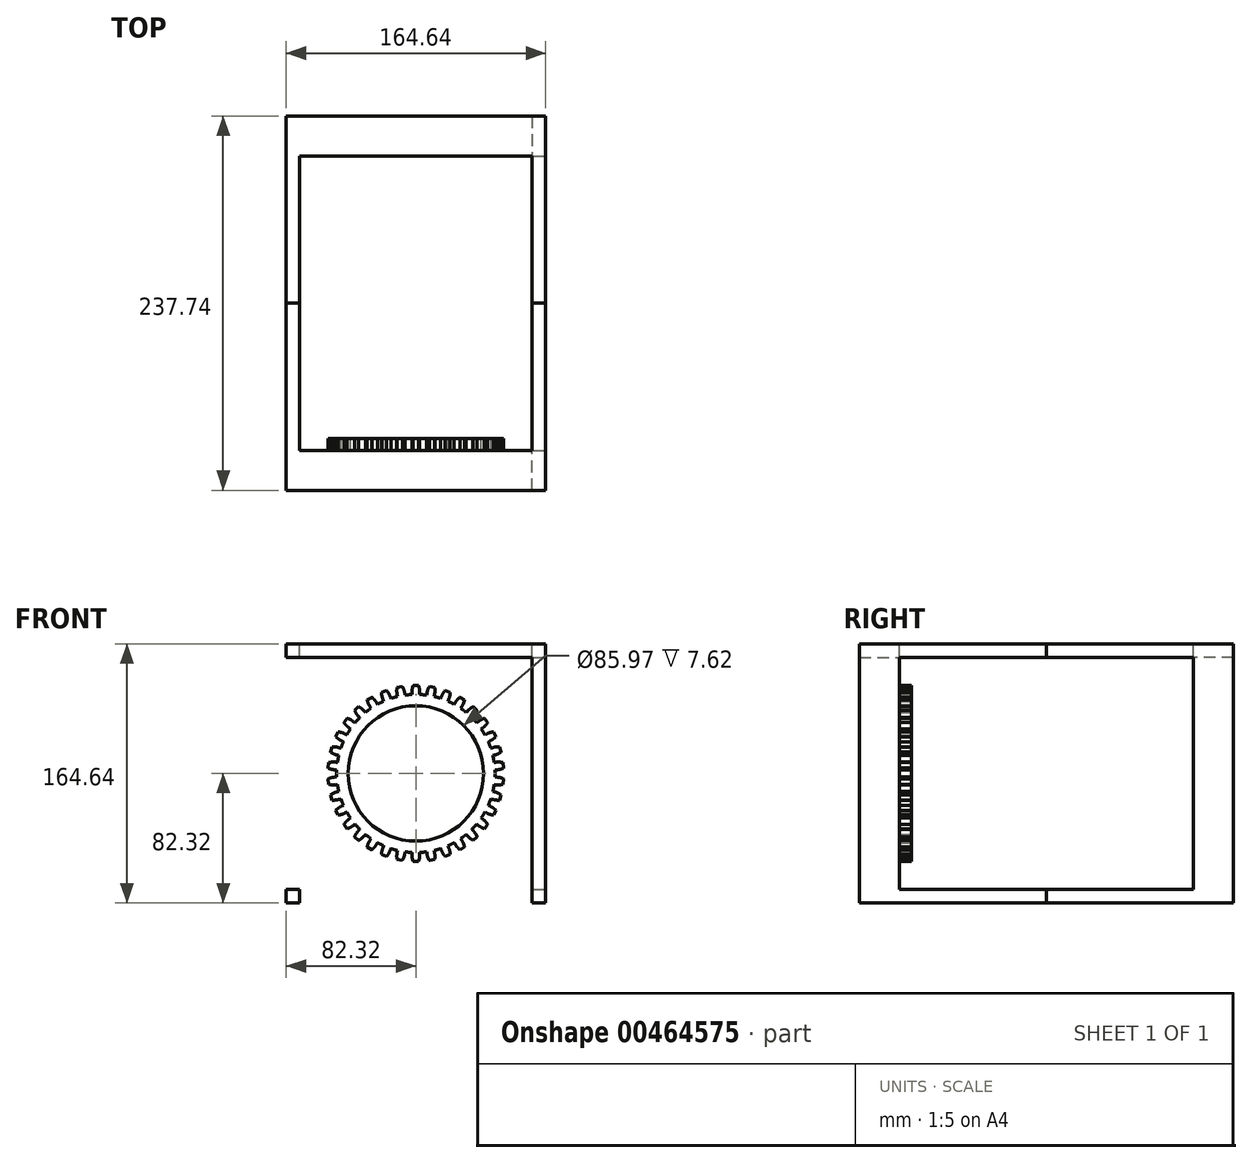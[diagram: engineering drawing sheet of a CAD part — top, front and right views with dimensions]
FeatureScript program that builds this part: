
annotation { "Feature Type Name" : "Feature", "Feature Type Description" : "" }
export const myFeature = defineFeature(function(context is Context, id is Id, definition is map)
    precondition{}
    {
        {
            var Q0;
            Q0=qCreatedBy(makeId("Front.planeOp"),FACE);
            var sketch = newSketch(context, id + "F0", { "sketchPlane" : qUnion([Q0])});
            skCircle(sketch, "E0", {"center": v(0, 0) * mm, "radius": 49.85 * mm});
            skLineSegment(sketch, "E1.bottom", {"start": v(-2.44, 49.79) * mm, "end": v(0, 49.79) * mm});
            skLineSegment(sketch, "E1.top", {"start": v(-2.44, 55.9) * mm, "end": v(0, 55.9) * mm});
            skLineSegment(sketch, "E1.left", {"start": v(-2.44, 49.79) * mm, "end": v(-2.44, 55.9) * mm});
            skLineSegment(sketch, "E1.right", {"start": v(0, 49.79) * mm, "end": v(0, 55.9) * mm});
            skFitSpline(sketch, "E2", {"points": [v(-1.74, 55.9) * mm, v(-2.44, 51.25) * mm], "startDerivative": vector(-1.37, -5.09) * mm, "endDerivative": vector(0, -7.68) * mm});
            skLineSegment(sketch, "E3.MirrorCS", {"start": v(2.44, 55.9) * mm, "end": v(0, 55.9) * mm});
            skFitSpline(sketch, "E4.MirrorCS", {"points": [v(1.74, 55.9) * mm, v(2.44, 51.25) * mm], "startDerivative": vector(1.37, -5.09) * mm, "endDerivative": vector(0, -7.68) * mm});
            skLineSegment(sketch, "E5.MirrorCS", {"start": v(2.44, 49.79) * mm, "end": v(2.44, 55.9) * mm});
            skCircle(sketch, "E6", {"center": v(0, 0) * mm, "radius": 50.24 * mm});
            skCircle(sketch, "E7", {"center": v(0, 0) * mm, "radius": 42.98 * mm});
            skSolve(sketch);
        }
        {
            var Q0;
            {var subQ5=sQuery(id+"F0.wireOp",EDGE,"E2");Q0=makeQuery(id+"F0.imprint","IMPRINT",FACE,{"disambiguationData":[TD([[makeQuery(id+"F0.imprint","IMPRINT",EDGE,{"derivedFrom":subQ5}),1.0]])]});}
            var Q1;
            {var subQ0=sQuery(id+"F0.wireOp",EDGE,"E4.MirrorCS");Q1=makeQuery(id+"F0.imprint","IMPRINT",FACE,{"disambiguationData":[TD([[makeQuery(id+"F0.imprint","IMPRINT",EDGE,{"derivedFrom":subQ0}),-1.0]])]});}
            extrude(context, id + "F1", {"entities" : qUnion([Q0, Q1]), "depth" : 7.62 * mm});
        }
        {
            var Q0;
            Q0=qCreatedBy(makeId("Top.planeOp"),FACE);
            var sketch = newSketch(context, id + "F2", { "sketchPlane" : qUnion([Q0])});
            skLineSegment(sketch, "E8", {"start": v(0, 0) * mm, "end": v(0, -26.55) * mm});
            skSolve(sketch);
        }
        {
            var Q0;
            Q0=makeQuery(id+"F1.opExtrude","SWEPT_BODY",BODY,{"disambiguationData":[OSD([sQuery(id+"F0.wireOp",EDGE,"E0"),sQuery(id+"F0.wireOp",EDGE,"E1.top"),sQuery(id+"F0.wireOp",EDGE,"E1.left"),sQuery(id+"F0.wireOp",EDGE,"E2"),sQuery(id+"F0.wireOp",EDGE,"E3.MirrorCS"),sQuery(id+"F0.wireOp",EDGE,"E4.MirrorCS"),sQuery(id+"F0.wireOp",EDGE,"E5.MirrorCS")])]});
            var Q1;
            Q1=sQuery(id+"F2.wireOp",EDGE,"E8");
            circularPattern(context, id + "F3", {"entities" : qUnion([Q0]), "axis" : qUnion([Q1]), "angle" : 360 * degree, "instanceCount" : 34, "equalSpace" : true});
        }
        {
            var Q0;
            {var subQ1=sQuery(id+"F0.wireOp",EDGE,"E0");var subQ3=sQuery(id+"F0.wireOp",EDGE,"E5.MirrorCS");var subQ4=makeQuery(id+"F0.imprint","INTERSECT",VERTEX,{"derivedFrom":[subQ1,subQ3]});Q0=makeQuery(id+"F0.imprint","IMPRINT",FACE,{"disambiguationData":[TD([[makeQuery(id+"F0.imprint","IMPRINT",EDGE,{"disambiguationData":[TD([[subQ4,-1.0]])],"derivedFrom":subQ3}),-1.0]])]});}
            var Q1;
            {var subQ4=sQuery(id+"F0.wireOp",EDGE,"E1.bottom");Q1=makeQuery(id+"F0.imprint","IMPRINT",FACE,{"disambiguationData":[TD([[makeQuery(id+"F0.imprint","IMPRINT",EDGE,{"derivedFrom":subQ4}),-1.0]])]});}
            var Q2;
            {var subQ1=sQuery(id+"F0.wireOp",EDGE,"E0");var subQ3=sQuery(id+"F0.wireOp",EDGE,"E1.right");var subQ4=makeQuery(id+"F0.imprint","INTERSECT",VERTEX,{"derivedFrom":[subQ1,subQ3]});Q2=makeQuery(id+"F0.imprint","IMPRINT",FACE,{"disambiguationData":[TD([[makeQuery(id+"F0.imprint","IMPRINT",EDGE,{"disambiguationData":[TD([[subQ4,-1.0]])],"derivedFrom":subQ3}),1.0]])]});}
            var Q3;
            {var subQ0=sQuery(id+"F0.wireOp",EDGE,"E5.MirrorCS");var subQ1=sQuery(id+"F0.wireOp",EDGE,"E0");var subQ2=makeQuery(id+"F0.imprint","INTERSECT",VERTEX,{"derivedFrom":[subQ1,subQ0]});Q3=makeQuery(id+"F0.imprint","IMPRINT",FACE,{"disambiguationData":[TD([[makeQuery(id+"F0.imprint","IMPRINT",EDGE,{"disambiguationData":[TD([[subQ2,-1.0]])],"derivedFrom":subQ1}),-1.0]])]});}
            var Q4;
            {var subQ0=sQuery(id+"F0.wireOp",EDGE,"E1.bottom");Q4=makeQuery(id+"F0.imprint","IMPRINT",FACE,{"disambiguationData":[TD([[makeQuery(id+"F0.imprint","IMPRINT",EDGE,{"derivedFrom":subQ0}),1.0]])]});}
            var Q5;
            Q5=makeQuery(id+"F3.opPattern","COPY",FACE,{"derivedFrom":makeQuery(id+"F1.opExtrude","CAP_FACE",FACE,{"disambiguationData":[OSD([sQuery(id+"F0.wireOp",EDGE,"E0"),sQuery(id+"F0.wireOp",EDGE,"E1.top"),sQuery(id+"F0.wireOp",EDGE,"E1.left"),sQuery(id+"F0.wireOp",EDGE,"E2"),sQuery(id+"F0.wireOp",EDGE,"E3.MirrorCS"),sQuery(id+"F0.wireOp",EDGE,"E4.MirrorCS"),sQuery(id+"F0.wireOp",EDGE,"E5.MirrorCS")])],"isStart":false}),"instanceName":"1"});
            extrude(context, id + "F4", {"entities" : qUnion([Q0, Q1, Q2, Q3, Q4]), "operationType" : NewBodyOperationType.ADD, "endBound" : BoundingType.UP_TO_SURFACE, "endBoundEntityFace" : qUnion([Q5]), "depth" : 25.4 * mm});
        }
        {
            var Q0;
            {var subQ0=sQuery(id+"F0.wireOp",EDGE,"E6");var subQ1=sQuery(id+"F0.wireOp",EDGE,"E5.MirrorCS");var subQ2=sQuery(id+"F0.wireOp",EDGE,"E4.MirrorCS");var subQ3=sQuery(id+"F0.wireOp",EDGE,"E3.MirrorCS");var subQ4=sQuery(id+"F0.wireOp",EDGE,"E2");var subQ5=sQuery(id+"F0.wireOp",EDGE,"E1.left");var subQ6=sQuery(id+"F0.wireOp",EDGE,"E1.top");var subQ7=makeQuery(id+"F1.opExtrude","CAP_FACE",FACE,{"disambiguationData":[OSD([subQ6,subQ5,subQ4,subQ3,subQ2,subQ1,subQ0])],"isStart":false});Q0=makeQuery(id+"F4.boolean.opBoolean","MERGE",FACE,{"derivedFrom":[subQ7,makeQuery(id+"F3.opPattern","COPY",FACE,{"derivedFrom":subQ7,"instanceName":"1"}),makeQuery(id+"F3.opPattern","COPY",FACE,{"derivedFrom":subQ7,"instanceName":"2"}),makeQuery(id+"F3.opPattern","COPY",FACE,{"derivedFrom":subQ7,"instanceName":"3"}),makeQuery(id+"F3.opPattern","COPY",FACE,{"derivedFrom":subQ7,"instanceName":"4"}),makeQuery(id+"F3.opPattern","COPY",FACE,{"derivedFrom":subQ7,"instanceName":"5"}),makeQuery(id+"F3.opPattern","COPY",FACE,{"derivedFrom":subQ7,"instanceName":"6"}),makeQuery(id+"F3.opPattern","COPY",FACE,{"derivedFrom":subQ7,"instanceName":"7"}),makeQuery(id+"F3.opPattern","COPY",FACE,{"derivedFrom":subQ7,"instanceName":"8"}),makeQuery(id+"F3.opPattern","COPY",FACE,{"derivedFrom":subQ7,"instanceName":"9"}),makeQuery(id+"F3.opPattern","COPY",FACE,{"derivedFrom":subQ7,"instanceName":"10"}),makeQuery(id+"F3.opPattern","COPY",FACE,{"derivedFrom":subQ7,"instanceName":"11"}),makeQuery(id+"F3.opPattern","COPY",FACE,{"derivedFrom":subQ7,"instanceName":"12"}),makeQuery(id+"F3.opPattern","COPY",FACE,{"derivedFrom":subQ7,"instanceName":"13"}),makeQuery(id+"F3.opPattern","COPY",FACE,{"derivedFrom":subQ7,"instanceName":"14"}),makeQuery(id+"F3.opPattern","COPY",FACE,{"derivedFrom":subQ7,"instanceName":"15"}),makeQuery(id+"F3.opPattern","COPY",FACE,{"derivedFrom":subQ7,"instanceName":"16"}),makeQuery(id+"F3.opPattern","COPY",FACE,{"derivedFrom":subQ7,"instanceName":"17"}),makeQuery(id+"F3.opPattern","COPY",FACE,{"derivedFrom":subQ7,"instanceName":"18"}),makeQuery(id+"F3.opPattern","COPY",FACE,{"derivedFrom":subQ7,"instanceName":"19"}),makeQuery(id+"F3.opPattern","COPY",FACE,{"derivedFrom":subQ7,"instanceName":"20"}),makeQuery(id+"F3.opPattern","COPY",FACE,{"derivedFrom":subQ7,"instanceName":"21"}),makeQuery(id+"F3.opPattern","COPY",FACE,{"derivedFrom":subQ7,"instanceName":"22"}),makeQuery(id+"F3.opPattern","COPY",FACE,{"derivedFrom":subQ7,"instanceName":"23"}),makeQuery(id+"F3.opPattern","COPY",FACE,{"derivedFrom":subQ7,"instanceName":"24"}),makeQuery(id+"F3.opPattern","COPY",FACE,{"derivedFrom":subQ7,"instanceName":"25"}),makeQuery(id+"F3.opPattern","COPY",FACE,{"derivedFrom":subQ7,"instanceName":"26"}),makeQuery(id+"F3.opPattern","COPY",FACE,{"derivedFrom":subQ7,"instanceName":"27"}),makeQuery(id+"F3.opPattern","COPY",FACE,{"derivedFrom":subQ7,"instanceName":"28"}),makeQuery(id+"F3.opPattern","COPY",FACE,{"derivedFrom":subQ7,"instanceName":"29"}),makeQuery(id+"F3.opPattern","COPY",FACE,{"derivedFrom":subQ7,"instanceName":"30"}),makeQuery(id+"F3.opPattern","COPY",FACE,{"derivedFrom":subQ7,"instanceName":"31"}),makeQuery(id+"F3.opPattern","COPY",FACE,{"derivedFrom":subQ7,"instanceName":"32"}),makeQuery(id+"F3.opPattern","COPY",FACE,{"derivedFrom":subQ7,"instanceName":"33"}),makeQuery(id+"F4.opExtrude","CAP_FACE",FACE,{"disambiguationData":[OSD([subQ6,subQ5,subQ4,subQ3,subQ2,subQ1,subQ0])],"isStart":false})]});}
            var sketch = newSketch(context, id + "F5", { "sketchPlane" : qUnion([Q0])});
            skLineSegment(sketch, "E9.bottom", {"start": v(0, 0) * mm, "end": v(-73.73, 0) * mm});
            skLineSegment(sketch, "E9.top", {"start": v(0, -73.73) * mm, "end": v(-73.73, -73.73) * mm});
            skLineSegment(sketch, "E9.left", {"start": v(0, 0) * mm, "end": v(0, -73.73) * mm});
            skLineSegment(sketch, "E9.right", {"start": v(-73.73, 0) * mm, "end": v(-73.73, -73.73) * mm});
            skLineSegment(sketch, "E10.bottom", {"start": v(-73.73, -73.73) * mm, "end": v(73.73, -73.73) * mm});
            skLineSegment(sketch, "E10.top", {"start": v(-73.73, 73.73) * mm, "end": v(73.73, 73.73) * mm});
            skLineSegment(sketch, "E10.left", {"start": v(-73.73, -73.73) * mm, "end": v(-73.73, 73.73) * mm});
            skLineSegment(sketch, "E10.right", {"start": v(73.73, -73.73) * mm, "end": v(73.73, 73.73) * mm});
            skLineSegment(sketch, "E11.bottom", {"start": v(-82.32, -82.32) * mm, "end": v(82.32, -82.32) * mm});
            skLineSegment(sketch, "E11.top", {"start": v(-82.32, 82.32) * mm, "end": v(82.32, 82.32) * mm});
            skLineSegment(sketch, "E11.left", {"start": v(-82.32, -82.32) * mm, "end": v(-82.32, 82.32) * mm});
            skLineSegment(sketch, "E11.right", {"start": v(82.32, -82.32) * mm, "end": v(82.32, 82.32) * mm});
            skLineSegment(sketch, "E12.bottom", {"start": v(-73.73, -73.73) * mm, "end": v(-82.32, -73.73) * mm});
            skLineSegment(sketch, "E12.top", {"start": v(-73.73, -82.32) * mm, "end": v(-82.32, -82.32) * mm});
            skLineSegment(sketch, "E12.left", {"start": v(-73.73, -73.73) * mm, "end": v(-73.73, -82.32) * mm});
            skLineSegment(sketch, "E12.right", {"start": v(-82.32, -73.73) * mm, "end": v(-82.32, -82.32) * mm});
            skLineSegment(sketch, "E13.bottom", {"start": v(-73.73, 73.73) * mm, "end": v(-82.32, 73.73) * mm});
            skLineSegment(sketch, "E13.top", {"start": v(-73.73, 82.32) * mm, "end": v(-82.32, 82.32) * mm});
            skLineSegment(sketch, "E13.left", {"start": v(-73.73, 73.73) * mm, "end": v(-73.73, 82.32) * mm});
            skLineSegment(sketch, "E13.right", {"start": v(-82.32, 73.73) * mm, "end": v(-82.32, 82.32) * mm});
            skLineSegment(sketch, "E14.bottom", {"start": v(73.73, 73.73) * mm, "end": v(82.32, 73.73) * mm});
            skLineSegment(sketch, "E14.top", {"start": v(73.73, 82.32) * mm, "end": v(82.32, 82.32) * mm});
            skLineSegment(sketch, "E14.left", {"start": v(73.73, 73.73) * mm, "end": v(73.73, 82.32) * mm});
            skLineSegment(sketch, "E14.right", {"start": v(82.32, 73.73) * mm, "end": v(82.32, 82.32) * mm});
            skLineSegment(sketch, "E15.bottom", {"start": v(73.73, -73.73) * mm, "end": v(82.32, -73.73) * mm});
            skLineSegment(sketch, "E15.top", {"start": v(73.73, -82.32) * mm, "end": v(82.32, -82.32) * mm});
            skLineSegment(sketch, "E15.left", {"start": v(73.73, -73.73) * mm, "end": v(73.73, -82.32) * mm});
            skLineSegment(sketch, "E15.right", {"start": v(82.32, -73.73) * mm, "end": v(82.32, -82.32) * mm});
            skSolve(sketch);
        }
        {
            var Q0;
            Q0=makeQuery(id+"F5.imprint","IMPRINT",FACE,{"disambiguationData":[TD([[makeQuery(id+"F5.imprint","IMPRINT",EDGE,{"derivedFrom":sQuery(id+"F5.wireOp",EDGE,"E12.bottom")}),1.0]])]});
            var Q1;
            Q1=makeQuery(id+"F5.imprint","IMPRINT",FACE,{"disambiguationData":[TD([[makeQuery(id+"F5.imprint","IMPRINT",EDGE,{"derivedFrom":sQuery(id+"F5.wireOp",EDGE,"E11.bottom")}),1.0]])]});
            var Q2;
            Q2=makeQuery(id+"F5.imprint","IMPRINT",FACE,{"disambiguationData":[TD([[makeQuery(id+"F5.imprint","IMPRINT",EDGE,{"derivedFrom":sQuery(id+"F5.wireOp",EDGE,"E11.left")}),-1.0]])]});
            var Q3;
            Q3=makeQuery(id+"F5.imprint","IMPRINT",FACE,{"disambiguationData":[TD([[makeQuery(id+"F5.imprint","IMPRINT",EDGE,{"derivedFrom":sQuery(id+"F5.wireOp",EDGE,"E10.right")}),-1.0]])]});
            var Q4;
            Q4=makeQuery(id+"F5.imprint","IMPRINT",FACE,{"disambiguationData":[TD([[makeQuery(id+"F5.imprint","IMPRINT",EDGE,{"derivedFrom":sQuery(id+"F5.wireOp",EDGE,"E15.bottom")}),-1.0]])]});
            var Q5;
            Q5=makeQuery(id+"F5.imprint","IMPRINT",FACE,{"disambiguationData":[TD([[makeQuery(id+"F5.imprint","IMPRINT",EDGE,{"derivedFrom":sQuery(id+"F5.wireOp",EDGE,"E10.top")}),1.0]])]});
            var Q6;
            Q6=makeQuery(id+"F5.imprint","IMPRINT",FACE,{"disambiguationData":[TD([[makeQuery(id+"F5.imprint","IMPRINT",EDGE,{"derivedFrom":sQuery(id+"F5.wireOp",EDGE,"E13.bottom")}),-1.0]])]});
            var Q7;
            Q7=makeQuery(id+"F5.imprint","IMPRINT",FACE,{"disambiguationData":[TD([[makeQuery(id+"F5.imprint","IMPRINT",EDGE,{"derivedFrom":sQuery(id+"F5.wireOp",EDGE,"E14.bottom")}),1.0]])]});
            extrude(context, id + "F6", {"entities" : qUnion([Q0, Q1, Q2, Q3, Q4, Q5, Q6, Q7]), "depth" : 25.4 * mm});
        }
        {
            var Q0;
            Q0=makeQuery(id+"F5.imprint","IMPRINT",FACE,{"disambiguationData":[TD([[makeQuery(id+"F5.imprint","IMPRINT",EDGE,{"derivedFrom":sQuery(id+"F5.wireOp",EDGE,"E12.bottom")}),1.0]])]});
            var Q1;
            Q1=makeQuery(id+"F5.imprint","IMPRINT",FACE,{"disambiguationData":[TD([[makeQuery(id+"F5.imprint","IMPRINT",EDGE,{"derivedFrom":sQuery(id+"F5.wireOp",EDGE,"E15.bottom")}),-1.0]])]});
            var Q2;
            Q2=makeQuery(id+"F5.imprint","IMPRINT",FACE,{"disambiguationData":[TD([[makeQuery(id+"F5.imprint","IMPRINT",EDGE,{"derivedFrom":sQuery(id+"F5.wireOp",EDGE,"E14.bottom")}),1.0]])]});
            var Q3;
            Q3=makeQuery(id+"F5.imprint","IMPRINT",FACE,{"disambiguationData":[TD([[makeQuery(id+"F5.imprint","IMPRINT",EDGE,{"derivedFrom":sQuery(id+"F5.wireOp",EDGE,"E13.bottom")}),-1.0]])]});
            extrude(context, id + "F7", {"entities" : qUnion([Q0, Q1, Q2, Q3]), "operationType" : NewBodyOperationType.ADD, "oppositeDirection" : true, "depth" : 93.47 * mm});
        }
        {
            var Q0;
            Q0=makeQuery(id+"F6.opExtrude","SWEPT_BODY",BODY,{"disambiguationData":[OSD([sQuery(id+"F5.wireOp",EDGE,"E10.bottom"),sQuery(id+"F5.wireOp",EDGE,"E10.top"),sQuery(id+"F5.wireOp",EDGE,"E10.left"),sQuery(id+"F5.wireOp",EDGE,"E10.right"),sQuery(id+"F5.wireOp",EDGE,"E11.bottom"),sQuery(id+"F5.wireOp",EDGE,"E11.top"),sQuery(id+"F5.wireOp",EDGE,"E11.left"),sQuery(id+"F5.wireOp",EDGE,"E11.right"),sQuery(id+"F5.wireOp",EDGE,"E12.top"),sQuery(id+"F5.wireOp",EDGE,"E12.right"),sQuery(id+"F5.wireOp",EDGE,"E13.top"),sQuery(id+"F5.wireOp",EDGE,"E13.right"),sQuery(id+"F5.wireOp",EDGE,"E14.top"),sQuery(id+"F5.wireOp",EDGE,"E14.right"),sQuery(id+"F5.wireOp",EDGE,"E15.top"),sQuery(id+"F5.wireOp",EDGE,"E15.right")])]});
            var Q1;
            Q1=makeQuery(id+"F7.opExtrude","CAP_FACE",FACE,{"disambiguationData":[OSD([sQuery(id+"F5.wireOp",EDGE,"E14.bottom"),sQuery(id+"F5.wireOp",EDGE,"E14.top"),sQuery(id+"F5.wireOp",EDGE,"E14.left"),sQuery(id+"F5.wireOp",EDGE,"E14.right")])],"isStart":false});
            mirror(context, id + "F8", {"operationType" : NewBodyOperationType.ADD, "entities" : qUnion([Q0]), "mirrorPlane" : qUnion([Q1])});
        }
    });
